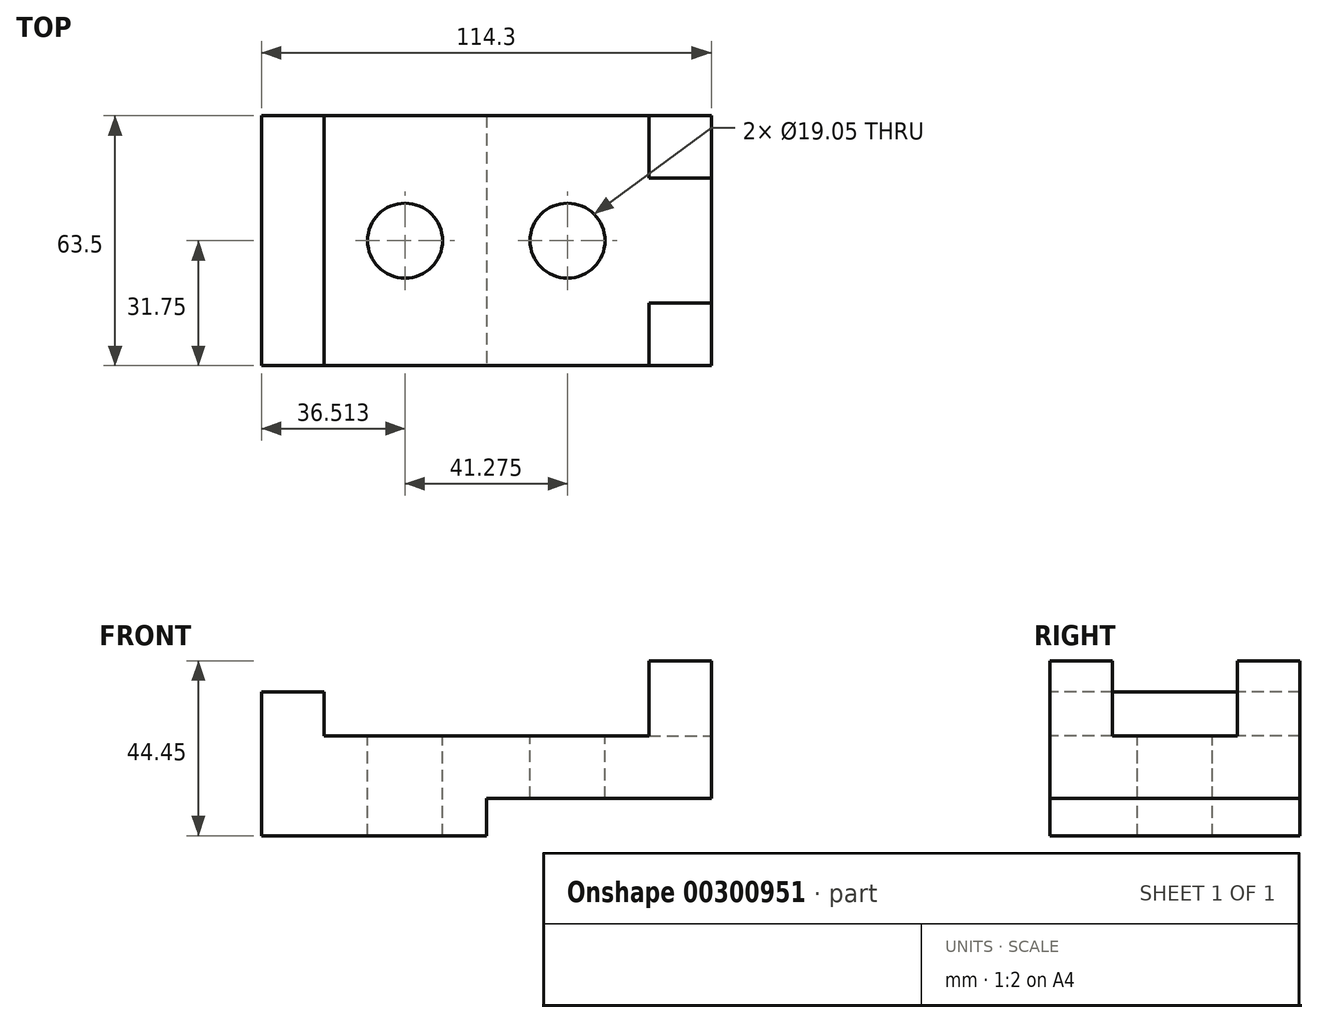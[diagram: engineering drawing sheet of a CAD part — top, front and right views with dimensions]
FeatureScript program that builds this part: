
annotation { "Feature Type Name" : "Feature", "Feature Type Description" : "" }
export const myFeature = defineFeature(function(context is Context, id is Id, definition is map)
    precondition{}
    {
        {
            var Q0;
            Q0=qCreatedBy(makeId("Front.planeOp"),FACE);
            var sketch = newSketch(context, id + "F0", { "sketchPlane" : qUnion([Q0])});
            skLineSegment(sketch, "E0.bottom", {"start": v(55.51, -41.9) * mm, "end": v(71.39, -41.9) * mm});
            skLineSegment(sketch, "E0.top", {"start": v(55.51, -78.4) * mm, "end": v(112.66, -78.4) * mm});
            skLineSegment(sketch, "E0.left", {"start": v(55.51, -41.9) * mm, "end": v(55.51, -78.4) * mm});
            skLineSegment(sketch, "E1.top", {"start": v(169.81, -68.88) * mm, "end": v(112.66, -68.88) * mm});
            skLineSegment(sketch, "E1.right", {"start": v(112.66, -78.4) * mm, "end": v(112.66, -68.88) * mm});
            skLineSegment(sketch, "E2.left", {"start": v(55.51, -41.9) * mm, "end": v(55.51, -60.95) * mm});
            skLineSegment(sketch, "E2.right", {"start": v(71.39, -41.9) * mm, "end": v(71.39, -53) * mm});
            skLineSegment(sketch, "E3", {"start": v(71.39, -53) * mm, "end": v(153.94, -53) * mm});
            skLineSegment(sketch, "E4", {"start": v(169.81, -68.88) * mm, "end": v(169.81, -53) * mm});
            skLineSegment(sketch, "E5.top", {"start": v(169.81, -33.96) * mm, "end": v(153.94, -33.96) * mm});
            skLineSegment(sketch, "E5.left", {"start": v(169.81, -53) * mm, "end": v(169.81, -33.96) * mm});
            skLineSegment(sketch, "E5.right", {"start": v(153.94, -53) * mm, "end": v(153.94, -33.96) * mm});
            skSolve(sketch);
        }
        {
            var Q0;
            Q0 = qSketchRegion(id + "F0", true);
            extrude(context, id + "F1", {"entities" : qUnion([Q0]), "oppositeDirection" : true, "depth" : 63.5 * mm});
        }
        {
            var Q0;
            Q0=makeQuery(id+"F1.opExtrude","SWEPT_FACE",FACE,{"disambiguationData":[OSD([sQuery(id+"F0.wireOp",EDGE,"E4"),sQuery(id+"F0.wireOp",EDGE,"E5.left")])]});
            var sketch = newSketch(context, id + "F2", { "sketchPlane" : qUnion([Q0])});
            skLineSegment(sketch, "E6.bottom", {"start": v(15.88, -33.96) * mm, "end": v(47.62, -33.96) * mm});
            skLineSegment(sketch, "E6.top", {"start": v(15.88, -53) * mm, "end": v(47.62, -53) * mm});
            skLineSegment(sketch, "E6.left", {"start": v(15.88, -33.96) * mm, "end": v(15.88, -53) * mm});
            skLineSegment(sketch, "E6.right", {"start": v(47.62, -33.96) * mm, "end": v(47.62, -53) * mm});
            skSolve(sketch);
        }
        {
            var Q0;
            Q0 = qSketchRegion(id + "F2", true);
            extrude(context, id + "F3", {"entities" : qUnion([Q0]), "operationType" : NewBodyOperationType.REMOVE, "oppositeDirection" : true, "depth" : 25.4 * mm});
        }
        {
            var Q0;
            Q0=makeQuery(id+"F3.boolean.opBoolean","MERGE",FACE,{"derivedFrom":[makeQuery(id+"F1.opExtrude","SWEPT_FACE",FACE,{"disambiguationData":[OSD([sQuery(id+"F0.wireOp",EDGE,"E3")])]}),makeQuery(id+"F3.opExtrude","SWEPT_FACE",FACE,{"disambiguationData":[OSD([sQuery(id+"F2.wireOp",EDGE,"E6.top")])]})]});
            var sketch = newSketch(context, id + "F4", { "sketchPlane" : qUnion([Q0])});
            skCircle(sketch, "E7", {"center": v(92.02, 31.75) * mm, "radius": 9.53 * mm});
            skCircle(sketch, "E8", {"center": v(133.3, 31.75) * mm, "radius": 9.53 * mm});
            skSolve(sketch);
        }
        {
            var Q0;
            Q0 = qSketchRegion(id + "F4", true);
            extrude(context, id + "F5", {"entities" : qUnion([Q0]), "operationType" : NewBodyOperationType.REMOVE, "endBound" : BoundingType.THROUGH_ALL, "oppositeDirection" : true, "depth" : 25.4 * mm});
        }
    });
